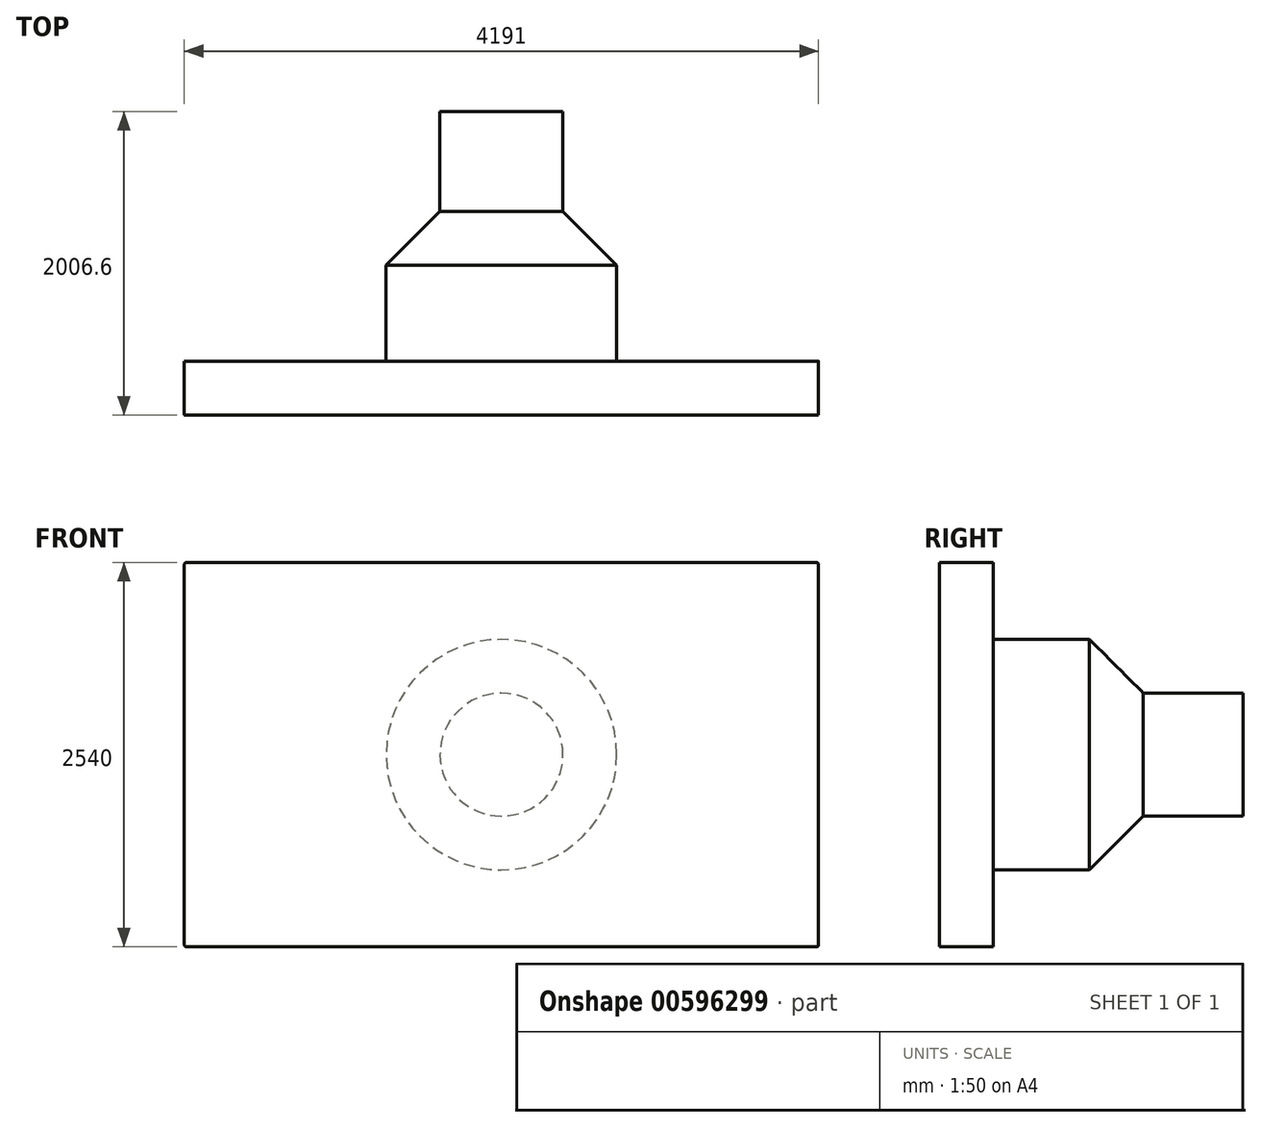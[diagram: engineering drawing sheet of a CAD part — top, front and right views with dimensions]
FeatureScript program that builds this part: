
annotation { "Feature Type Name" : "Feature", "Feature Type Description" : "" }
export const myFeature = defineFeature(function(context is Context, id is Id, definition is map)
    precondition{}
    {
        {
            var Q0;
            Q0=qCreatedBy(makeId("Top.planeOp"),FACE);
            var sketch = newSketch(context, id + "F0", { "sketchPlane" : qUnion([Q0])});
            skLineSegment(sketch, "E0", {"start": v(0, 0) * mm, "end": v(762, 0) * mm});
            skLineSegment(sketch, "E1", {"start": v(762, 0) * mm, "end": v(762, 635) * mm});
            skLineSegment(sketch, "E2", {"start": v(762, 635) * mm, "end": v(406.4, 990.6) * mm});
            skLineSegment(sketch, "E3", {"start": v(406.4, 990.6) * mm, "end": v(406.4, 1651) * mm});
            skLineSegment(sketch, "E4", {"start": v(406.4, 1651) * mm, "end": v(0, 1651) * mm});
            skLineSegment(sketch, "E5", {"start": v(0, 1651) * mm, "end": v(0, 0) * mm});
            skSolve(sketch);
        }
        {
            var Q0;
            Q0 = qSketchRegion(id + "F0", true);
            var Q1;
            Q1=sQuery(id+"F0.wireOp",EDGE,"E5");
            revolve(context, id + "F1", {"entities" : qUnion([Q0]), "axis" : qUnion([Q1]), "revolveType" : RevolveType.FULL});
        }
        {
            var Q0;
            Q0=makeQuery(id+"F1.opRevolve","SWEPT_FACE",FACE,{"disambiguationData":[OSD([sQuery(id+"F0.wireOp",EDGE,"E0")])]});
            var sketch = newSketch(context, id + "F2", { "sketchPlane" : qUnion([Q0])});
            skLineSegment(sketch, "E6.bottom", {"start": v(2095.5, 1270) * mm, "end": v(-2095.5, 1270) * mm});
            skLineSegment(sketch, "E6.top", {"start": v(2095.5, -1270) * mm, "end": v(-2095.5, -1270) * mm});
            skLineSegment(sketch, "E6.left", {"start": v(2095.5, 1270) * mm, "end": v(2095.5, -1270) * mm});
            skLineSegment(sketch, "E6.right", {"start": v(-2095.5, 1270) * mm, "end": v(-2095.5, -1270) * mm});
            skPoint(sketch, "E6.middle", {"position": v(0, 0) * mm});
            skSolve(sketch);
        }
        {
            var Q0;
            Q0 = qSketchRegion(id + "F2", true);
            extrude(context, id + "F3", {"entities" : qUnion([Q0]), "operationType" : NewBodyOperationType.ADD, "depth" : 355.6 * mm, "offsetDistance" : 25.4 * mm});
        }
        {
            var Q0;
            Q0=makeQuery(id+"F3.opExtrude","SWEPT_EDGE",EDGE,{"disambiguationData":[OSD([sQuery(id+"F2.wireOp",EDGE,"E6.top"),sQuery(id+"F2.wireOp",EDGE,"E6.right")])]});
            var Q1;
            Q1=makeQuery(id+"F3.opExtrude","SWEPT_EDGE",EDGE,{"disambiguationData":[OSD([sQuery(id+"F2.wireOp",EDGE,"E6.bottom"),sQuery(id+"F2.wireOp",EDGE,"E6.right")])]});
            var Q2;
            Q2=makeQuery(id+"F3.opExtrude","SWEPT_EDGE",EDGE,{"disambiguationData":[OSD([sQuery(id+"F2.wireOp",EDGE,"E6.bottom"),sQuery(id+"F2.wireOp",EDGE,"E6.left")])]});
            var Q3;
            Q3=makeQuery(id+"F3.opExtrude","SWEPT_EDGE",EDGE,{"disambiguationData":[OSD([sQuery(id+"F2.wireOp",EDGE,"E6.top"),sQuery(id+"F2.wireOp",EDGE,"E6.left")])]});
            fillet(context, id + "F4", {"entities" : qUnion([Q0, Q1, Q2, Q3]), "radius" : 12.7 * mm, "tangentPropagation" : true, "allowEdgeOverflow" : false});
        }
    });
